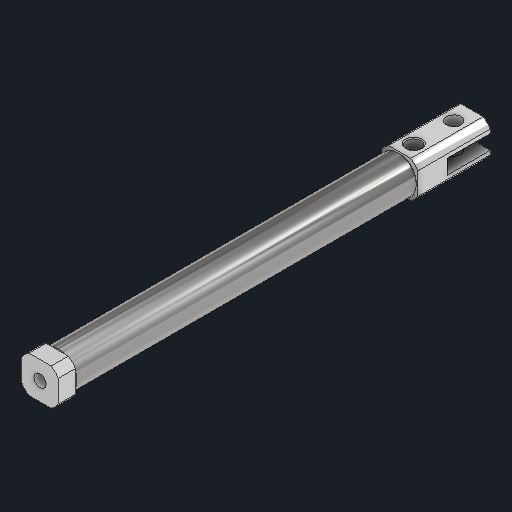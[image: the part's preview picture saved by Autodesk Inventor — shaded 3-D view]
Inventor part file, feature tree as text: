
AUTODESK INVENTOR PART (.ipt)
format: ipt  version: 2024 (Build 280153000, 153)  size: 188,416 bytes
history: native  units: in
note: dims shown in document units (in); Inventor stores cm internally (conversion verified against a paired STEP export)
features: extrude x1, thread x1, other x1
ambient origin geometry x8: Origin, YZ Plane, XZ Plane, XY Plane, X Axis, Y Axis, Z Axis, Center Point
bodies: Solid1 (feature_tree)
feature tree (3):
  extrude  "Extrusion3"  TaperAngle=0.0deg  [1 undecoded]
  thread  "Thread1"  [1 undecoded]
  other  "D-ClevisPinDetail"
note: 2 required parameter values undecoded (feature->parameter linkage not recoverable at this tier; creation-order binding heuristic only, values carry confidence <= 0.55)
